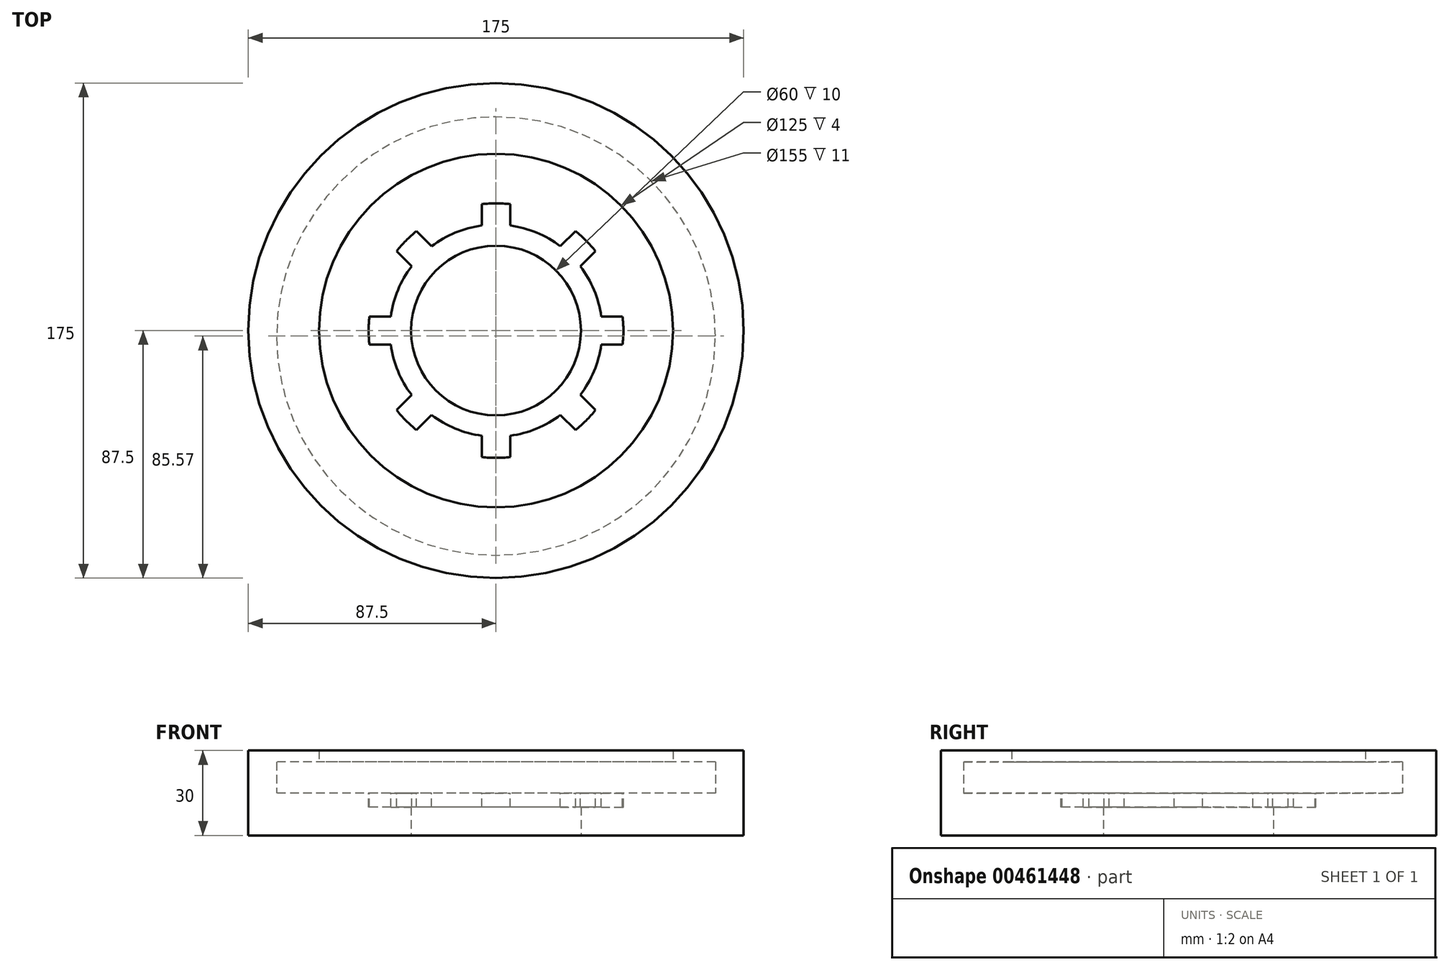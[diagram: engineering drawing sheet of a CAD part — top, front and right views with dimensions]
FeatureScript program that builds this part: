
annotation { "Feature Type Name" : "Feature", "Feature Type Description" : "" }
export const myFeature = defineFeature(function(context is Context, id is Id, definition is map)
    precondition{}
    {
        {
            var Q0;
            Q0=qCreatedBy(makeId("Top.planeOp"),FACE);
            var sketch = newSketch(context, id + "F0", { "sketchPlane" : qUnion([Q0])});
            skCircle(sketch, "E0", {"center": v(0, 0) * mm, "radius": 87.5 * mm});
            skCircle(sketch, "E1", {"center": v(0, 0) * mm, "radius": 30 * mm});
            skSolve(sketch);
        }
        {
            var Q0;
            Q0=makeQuery(id+"F0.imprint","IMPRINT",FACE,{"disambiguationData":[TD([[makeQuery(id+"F0.imprint","IMPRINT",EDGE,{"derivedFrom":sQuery(id+"F0.wireOp",EDGE,"E0")}),1.0]])]});
            extrude(context, id + "F1", {"entities" : qUnion([Q0]), "depth" : 10 * mm});
        }
        {
            var Q0;
            Q0=makeQuery(id+"F1.opExtrude","CAP_FACE",FACE,{"disambiguationData":[OSD([sQuery(id+"F0.wireOp",EDGE,"E0"),sQuery(id+"F0.wireOp",EDGE,"E1")])],"isStart":false});
            var sketch = newSketch(context, id + "F2", { "sketchPlane" : qUnion([Q0])});
            skCircle(sketch, "E2", {"center": v(0, 0) * mm, "radius": 37.5 * mm});
            skSolve(sketch);
        }
        {
            var Q0;
            Q0=makeQuery(id+"F2.imprint","IMPRINT",FACE,{"disambiguationData":[TD([[makeQuery(id+"F2.imprint","IMPRINT",EDGE,{"derivedFrom":sQuery(id+"F2.wireOp",EDGE,"E2")}),-1.0]])]});
            extrude(context, id + "F3", {"entities" : qUnion([Q0]), "operationType" : NewBodyOperationType.ADD, "depth" : 5 * mm});
        }
        {
            var Q0;
            Q0=makeQuery(id+"F3.opExtrude","CAP_FACE",FACE,{"disambiguationData":[OSD([sQuery(id+"F0.wireOp",EDGE,"E0"),sQuery(id+"F2.wireOp",EDGE,"E2")])],"isStart":false});
            var sketch = newSketch(context, id + "F4", { "sketchPlane" : qUnion([Q0])});
            skLineSegment(sketch, "E3", {"start": v(0, -87.5) * mm, "end": v(0, 87.5) * mm, "construction": true});
            skLineSegment(sketch, "E4", {"start": v(-87.5, 0) * mm, "end": v(87.5, 0) * mm, "construction": true});
            skLineSegment(sketch, "E5", {"start": v(0, 0) * mm, "end": v(61.87, -61.87) * mm, "construction": true});
            skLineSegment(sketch, "E6", {"start": v(0, 0) * mm, "end": v(-61.87, -61.87) * mm, "construction": true});
            skLineSegment(sketch, "E7", {"start": v(0, 0) * mm, "end": v(-61.87, 61.87) * mm, "construction": true});
            skLineSegment(sketch, "E8", {"start": v(0, 0) * mm, "end": v(61.87, 61.87) * mm, "construction": true});
            skLineSegment(sketch, "E9", {"start": v(-22.74, 29.82) * mm, "end": v(-58.24, 65.3) * mm});
            skLineSegment(sketch, "E10", {"start": v(-29.82, 22.74) * mm, "end": v(-65.3, 58.24) * mm});
            skLineSegment(sketch, "E11", {"start": v(-5, 37.17) * mm, "end": v(-5, 87.36) * mm});
            skLineSegment(sketch, "E12", {"start": v(5, 37.17) * mm, "end": v(5, 87.36) * mm});
            skLineSegment(sketch, "E13", {"start": v(22.74, 29.82) * mm, "end": v(58.24, 65.3) * mm});
            skLineSegment(sketch, "E14", {"start": v(29.82, 22.74) * mm, "end": v(65.3, 58.24) * mm});
            skLineSegment(sketch, "E15", {"start": v(37.17, 5) * mm, "end": v(87.36, 5) * mm});
            skLineSegment(sketch, "E16", {"start": v(37.17, -5) * mm, "end": v(87.36, -5) * mm});
            skLineSegment(sketch, "E17", {"start": v(29.82, -22.74) * mm, "end": v(65.3, -58.24) * mm});
            skLineSegment(sketch, "E18", {"start": v(22.74, -29.82) * mm, "end": v(58.24, -65.3) * mm});
            skLineSegment(sketch, "E19", {"start": v(5, -37.17) * mm, "end": v(5, -87.36) * mm});
            skLineSegment(sketch, "E20", {"start": v(-5, -37.17) * mm, "end": v(-5, -87.36) * mm});
            skLineSegment(sketch, "E21", {"start": v(-29.82, -22.74) * mm, "end": v(-65.3, -58.24) * mm});
            skLineSegment(sketch, "E22", {"start": v(-22.74, -29.82) * mm, "end": v(-58.24, -65.3) * mm});
            skLineSegment(sketch, "E23", {"start": v(-37.17, -5) * mm, "end": v(-87.36, -5) * mm});
            skLineSegment(sketch, "E24", {"start": v(-37.17, 5) * mm, "end": v(-87.36, 5) * mm});
            skCircle(sketch, "E25", {"center": v(0, 0) * mm, "radius": 45 * mm});
            skSolve(sketch);
        }
        {
            var Q0;
            {var subQ0=sQuery(id+"F4.wireOp",EDGE,"E9");var subQ1=makeQuery(id+"F3.opExtrude","CAP_EDGE",EDGE,{"disambiguationData":[OSD([sQuery(id+"F2.wireOp",EDGE,"E2")])],"isStart":false});var subQ2=makeQuery(id+"F4.imprint","INTERSECT",VERTEX,{"derivedFrom":[subQ1,subQ0]});Q0=makeQuery(id+"F4.imprint","IMPRINT",FACE,{"disambiguationData":[TD([[makeQuery(id+"F4.imprint","IMPRINT",EDGE,{"disambiguationData":[TD([[subQ2,-1.0]])],"derivedFrom":subQ0}),1.0]])]});}
            var Q1;
            {var subQ0=sQuery(id+"F4.wireOp",EDGE,"E11");var subQ1=makeQuery(id+"F3.opExtrude","CAP_EDGE",EDGE,{"disambiguationData":[OSD([sQuery(id+"F2.wireOp",EDGE,"E2")])],"isStart":false});var subQ2=makeQuery(id+"F4.imprint","INTERSECT",VERTEX,{"derivedFrom":[subQ1,subQ0]});Q1=makeQuery(id+"F4.imprint","IMPRINT",FACE,{"disambiguationData":[TD([[makeQuery(id+"F4.imprint","IMPRINT",EDGE,{"disambiguationData":[TD([[subQ2,-1.0]])],"derivedFrom":subQ0}),-1.0]])]});}
            var Q2;
            {var subQ0=sQuery(id+"F4.wireOp",EDGE,"E13");var subQ1=makeQuery(id+"F3.opExtrude","CAP_EDGE",EDGE,{"disambiguationData":[OSD([sQuery(id+"F2.wireOp",EDGE,"E2")])],"isStart":false});var subQ2=makeQuery(id+"F4.imprint","INTERSECT",VERTEX,{"derivedFrom":[subQ1,subQ0]});Q2=makeQuery(id+"F4.imprint","IMPRINT",FACE,{"disambiguationData":[TD([[makeQuery(id+"F4.imprint","IMPRINT",EDGE,{"disambiguationData":[TD([[subQ2,-1.0]])],"derivedFrom":subQ0}),-1.0]])]});}
            var Q3;
            {var subQ0=sQuery(id+"F4.wireOp",EDGE,"E15");var subQ1=makeQuery(id+"F3.opExtrude","CAP_EDGE",EDGE,{"disambiguationData":[OSD([sQuery(id+"F2.wireOp",EDGE,"E2")])],"isStart":false});var subQ2=makeQuery(id+"F4.imprint","INTERSECT",VERTEX,{"derivedFrom":[subQ1,subQ0]});Q3=makeQuery(id+"F4.imprint","IMPRINT",FACE,{"disambiguationData":[TD([[makeQuery(id+"F4.imprint","IMPRINT",EDGE,{"disambiguationData":[TD([[subQ2,-1.0]])],"derivedFrom":subQ0}),-1.0]])]});}
            var Q4;
            {var subQ0=sQuery(id+"F4.wireOp",EDGE,"E17");var subQ1=makeQuery(id+"F3.opExtrude","CAP_EDGE",EDGE,{"disambiguationData":[OSD([sQuery(id+"F2.wireOp",EDGE,"E2")])],"isStart":false});var subQ2=makeQuery(id+"F4.imprint","INTERSECT",VERTEX,{"derivedFrom":[subQ1,subQ0]});Q4=makeQuery(id+"F4.imprint","IMPRINT",FACE,{"disambiguationData":[TD([[makeQuery(id+"F4.imprint","IMPRINT",EDGE,{"disambiguationData":[TD([[subQ2,-1.0]])],"derivedFrom":subQ0}),-1.0]])]});}
            var Q5;
            {var subQ0=sQuery(id+"F4.wireOp",EDGE,"E19");var subQ1=makeQuery(id+"F3.opExtrude","CAP_EDGE",EDGE,{"disambiguationData":[OSD([sQuery(id+"F2.wireOp",EDGE,"E2")])],"isStart":false});var subQ2=makeQuery(id+"F4.imprint","INTERSECT",VERTEX,{"derivedFrom":[subQ1,subQ0]});Q5=makeQuery(id+"F4.imprint","IMPRINT",FACE,{"disambiguationData":[TD([[makeQuery(id+"F4.imprint","IMPRINT",EDGE,{"disambiguationData":[TD([[subQ2,-1.0]])],"derivedFrom":subQ0}),-1.0]])]});}
            var Q6;
            {var subQ0=sQuery(id+"F4.wireOp",EDGE,"E21");var subQ1=makeQuery(id+"F3.opExtrude","CAP_EDGE",EDGE,{"disambiguationData":[OSD([sQuery(id+"F2.wireOp",EDGE,"E2")])],"isStart":false});var subQ2=makeQuery(id+"F4.imprint","INTERSECT",VERTEX,{"derivedFrom":[subQ1,subQ0]});Q6=makeQuery(id+"F4.imprint","IMPRINT",FACE,{"disambiguationData":[TD([[makeQuery(id+"F4.imprint","IMPRINT",EDGE,{"disambiguationData":[TD([[subQ2,-1.0]])],"derivedFrom":subQ0}),1.0]])]});}
            var Q7;
            {var subQ0=sQuery(id+"F4.wireOp",EDGE,"E23");var subQ1=makeQuery(id+"F3.opExtrude","CAP_EDGE",EDGE,{"disambiguationData":[OSD([sQuery(id+"F2.wireOp",EDGE,"E2")])],"isStart":false});var subQ2=makeQuery(id+"F4.imprint","INTERSECT",VERTEX,{"derivedFrom":[subQ1,subQ0]});Q7=makeQuery(id+"F4.imprint","IMPRINT",FACE,{"disambiguationData":[TD([[makeQuery(id+"F4.imprint","IMPRINT",EDGE,{"disambiguationData":[TD([[subQ2,-1.0]])],"derivedFrom":subQ0}),-1.0]])]});}
            extrude(context, id + "F5", {"entities" : qUnion([Q0, Q1, Q2, Q3, Q4, Q5, Q6, Q7]), "operationType" : NewBodyOperationType.REMOVE, "oppositeDirection" : true, "depth" : 5 * mm});
        }
        {
            var Q0;
            Q0=makeQuery(id+"F3.opExtrude","CAP_FACE",FACE,{"disambiguationData":[OSD([sQuery(id+"F0.wireOp",EDGE,"E0"),sQuery(id+"F2.wireOp",EDGE,"E2")])],"isStart":false});
            var sketch = newSketch(context, id + "F6", { "sketchPlane" : qUnion([Q0])});
            skCircle(sketch, "E26", {"center": v(0, 0) * mm, "radius": 62.5 * mm});
            skSolve(sketch);
        }
        {
            var Q0;
            Q0=makeQuery(id+"F6.imprint","IMPRINT",FACE,{"disambiguationData":[TD([[makeQuery(id+"F6.imprint","IMPRINT",EDGE,{"derivedFrom":sQuery(id+"F6.wireOp",EDGE,"E26")}),-1.0]])]});
            extrude(context, id + "F7", {"entities" : qUnion([Q0]), "operationType" : NewBodyOperationType.ADD, "depth" : 15 * mm});
        }
        {
            var Q0;
            Q0=makeQuery(id+"F3.opExtrude","CAP_FACE",FACE,{"disambiguationData":[OSD([sQuery(id+"F0.wireOp",EDGE,"E0"),sQuery(id+"F2.wireOp",EDGE,"E2")])],"isStart":false});
            var sketch = newSketch(context, id + "F8", { "sketchPlane" : qUnion([Q0])});
            skCircle(sketch, "E27", {"center": v(0, -1.93) * mm, "radius": 77.5 * mm});
            skSolve(sketch);
        }
        {
            var Q0;
            Q0=qSketchRegion(id+"F8",true);
            extrude(context, id + "F9", {"entities" : qUnion([Q0]), "operationType" : NewBodyOperationType.REMOVE, "depth" : 11 * mm});
        }
    });
